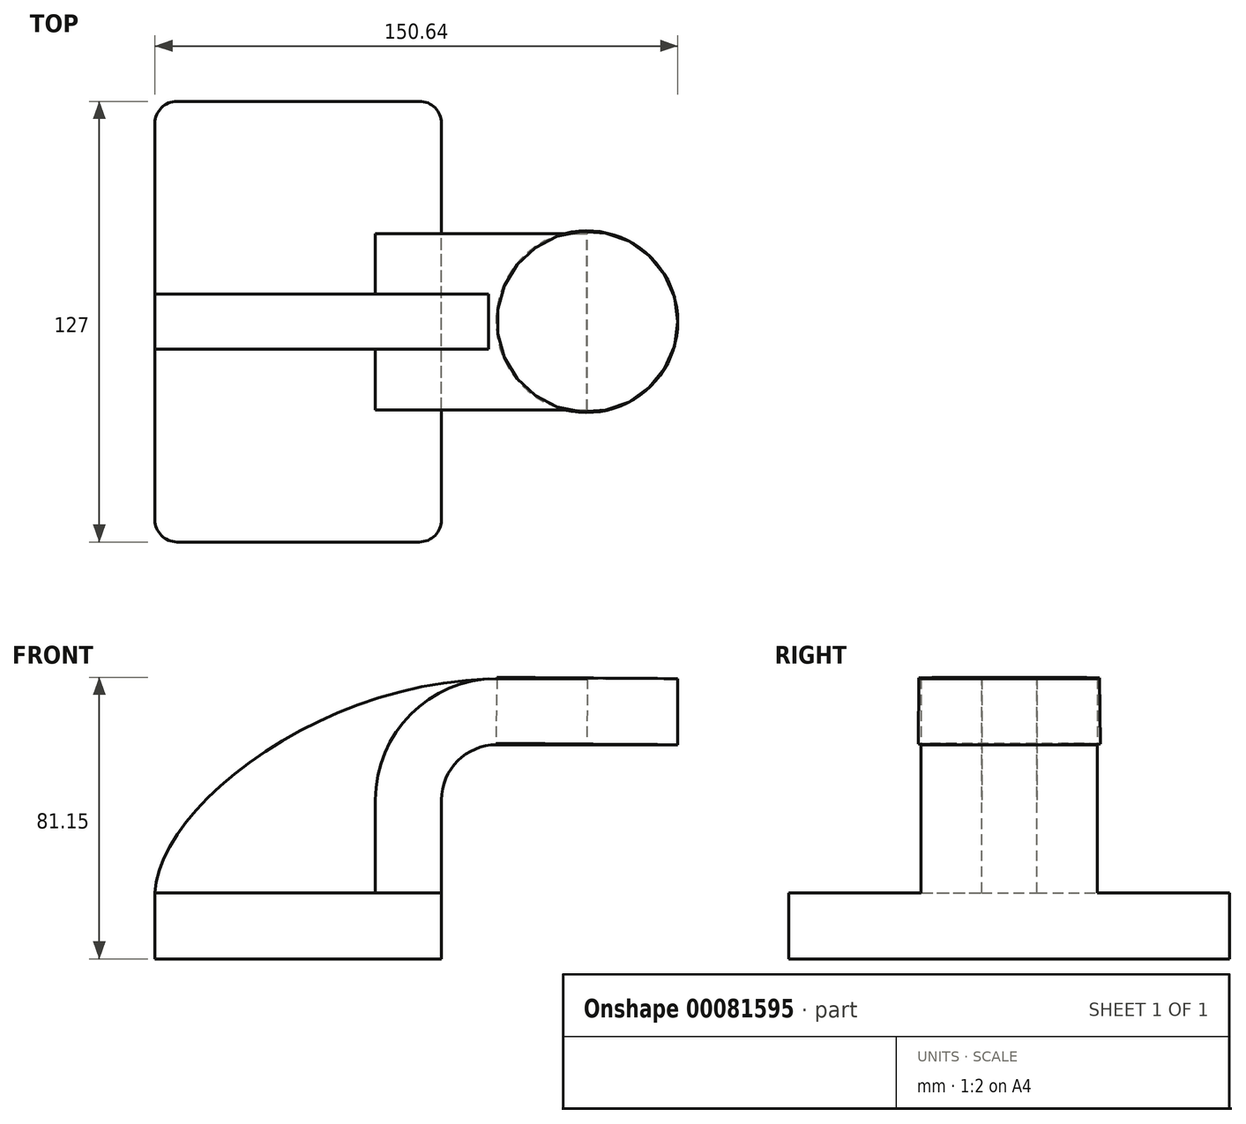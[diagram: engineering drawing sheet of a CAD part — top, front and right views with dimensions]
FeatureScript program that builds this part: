
annotation { "Feature Type Name" : "Feature", "Feature Type Description" : "" }
export const myFeature = defineFeature(function(context is Context, id is Id, definition is map)
    precondition{}
    {
        {
            var Q0;
            Q0=qCreatedBy(makeId("Front.planeOp"),FACE);
            var sketch = newSketch(context, id + "F0", { "sketchPlane" : qUnion([Q0])});
            skLineSegment(sketch, "E0.bottom", {"start": v(-41.28, 9.52) * mm, "end": v(41.27, 9.53) * mm});
            skLineSegment(sketch, "E0.top", {"start": v(-41.28, -9.53) * mm, "end": v(41.28, -9.53) * mm});
            skLineSegment(sketch, "E0.left", {"start": v(-41.28, 9.52) * mm, "end": v(-41.27, -9.53) * mm});
            skLineSegment(sketch, "E0.right", {"start": v(41.28, 9.53) * mm, "end": v(41.28, -9.52) * mm});
            skPoint(sketch, "E0.middle", {"position": v(0, 0) * mm});
            skLineSegment(sketch, "E1", {"start": v(41.27, 9.53) * mm, "end": v(41.27, 36.3) * mm});
            skArc(sketch, "E2", {"start": v(41.27, 36.3) * mm, "mid": v(45.92, 47.52) * mm, "end": v(57.15, 52.17) * mm});
            skLineSegment(sketch, "E3", {"start": v(57.15, 52.17) * mm, "end": v(83.15, 52.17) * mm});
            skLineSegment(sketch, "E4.0", {"start": v(57.15, 71.22) * mm, "end": v(83.3, 71.22) * mm});
            skArc(sketch, "E4.1", {"start": v(22.23, 36.3) * mm, "mid": v(32.45, 61) * mm, "end": v(57.15, 71.22) * mm});
            skLineSegment(sketch, "E4.2", {"start": v(22.22, 9.53) * mm, "end": v(22.22, 36.3) * mm});
            skFitSpline(sketch, "E5", {"points": [v(-41.28, 9.53) * mm, v(54.82, 71.14) * mm], "startDerivative": vector(2.49, 71.55) * mm, "endDerivative": vector(151, 4.8) * mm});
            skLineSegment(sketch, "E6", {"start": v(83.3, 71.22) * mm, "end": v(83.15, 52.17) * mm});
            skLineSegment(sketch, "E7.bottom", {"start": v(109.36, 71.22) * mm, "end": v(57.1, 71.22) * mm});
            skLineSegment(sketch, "E7.top", {"start": v(109.36, 52.17) * mm, "end": v(57.1, 52.17) * mm});
            skLineSegment(sketch, "E7.left", {"start": v(109.36, 71.22) * mm, "end": v(109.36, 52.17) * mm});
            skLineSegment(sketch, "E7.right", {"start": v(57.1, 71.22) * mm, "end": v(57.1, 52.17) * mm});
            skPoint(sketch, "E7.middle", {"position": v(83.23, 61.7) * mm});
            skSolve(sketch);
        }
        {
            var Q0;
            Q0=makeQuery(id+"F0.imprint","IMPRINT",FACE,{"disambiguationData":[TD([[makeQuery(id+"F0.imprint","IMPRINT",EDGE,{"derivedFrom":sQuery(id+"F0.wireOp",EDGE,"E0.top")}),1.0]])]});
            extrude(context, id + "F1", {"entities" : qUnion([Q0]), "endBound" : BoundingType.SYMMETRIC, "depth" : 127 * mm});
        }
        {
            var Q0;
            {var subQ0=sQuery(id+"F0.wireOp",EDGE,"E1");Q0=makeQuery(id+"F0.imprint","IMPRINT",FACE,{"disambiguationData":[TD([[makeQuery(id+"F0.imprint","IMPRINT",EDGE,{"derivedFrom":subQ0}),1.0]])]});}
            var Q1;
            {var subQ0=sQuery(id+"F0.wireOp",EDGE,"E6");Q1=makeQuery(id+"F0.imprint","IMPRINT",FACE,{"disambiguationData":[TD([[makeQuery(id+"F0.imprint","IMPRINT",EDGE,{"derivedFrom":subQ0}),-1.0]])]});}
            extrude(context, id + "F2", {"entities" : qUnion([Q0, Q1]), "operationType" : NewBodyOperationType.ADD, "endBound" : BoundingType.SYMMETRIC, "depth" : 50.8 * mm});
        }
        {
            var Q0;
            {var subQ2=sQuery(id+"F0.wireOp",EDGE,"E4.2");Q0=makeQuery(id+"F0.imprint","IMPRINT",FACE,{"disambiguationData":[TD([[makeQuery(id+"F0.imprint","IMPRINT",EDGE,{"derivedFrom":subQ2}),1.0]])]});}
            extrude(context, id + "F3", {"entities" : qUnion([Q0]), "operationType" : NewBodyOperationType.ADD, "endBound" : BoundingType.SYMMETRIC, "depth" : 15.88 * mm});
        }
        {
            var Q0;
            {var subQ0=sQuery(id+"F0.wireOp",EDGE,"E6");Q0=makeQuery(id+"F0.imprint","IMPRINT",FACE,{"disambiguationData":[TD([[makeQuery(id+"F0.imprint","IMPRINT",EDGE,{"derivedFrom":subQ0}),1.0]])]});}
            var Q1;
            Q1=sQuery(id+"F0.wireOp",EDGE,"E6");
            revolve(context, id + "F4", {"entities" : qUnion([Q0]), "axis" : qUnion([Q1]), "revolveType" : RevolveType.FULL});
        }
        {
            var Q0;
            Q0=makeQuery(id+"F1.opExtrude","CAP_EDGE",EDGE,{"disambiguationData":[OSD([sQuery(id+"F0.wireOp",EDGE,"E0.right")])],"isStart":false});
            var Q1;
            Q1=makeQuery(id+"F1.opExtrude","CAP_EDGE",EDGE,{"disambiguationData":[OSD([sQuery(id+"F0.wireOp",EDGE,"E0.left")])],"isStart":false});
            var Q2;
            Q2=makeQuery(id+"F1.opExtrude","CAP_EDGE",EDGE,{"disambiguationData":[OSD([sQuery(id+"F0.wireOp",EDGE,"E0.right")])],"isStart":true});
            var Q3;
            Q3=makeQuery(id+"F1.opExtrude","CAP_EDGE",EDGE,{"disambiguationData":[OSD([sQuery(id+"F0.wireOp",EDGE,"E0.left")])],"isStart":true});
            fillet(context, id + "F5", {"entities" : qUnion([Q0, Q1, Q2, Q3]), "radius" : 6.35 * mm, "tangentPropagation" : true, "allowEdgeOverflow" : false});
        }
    });
